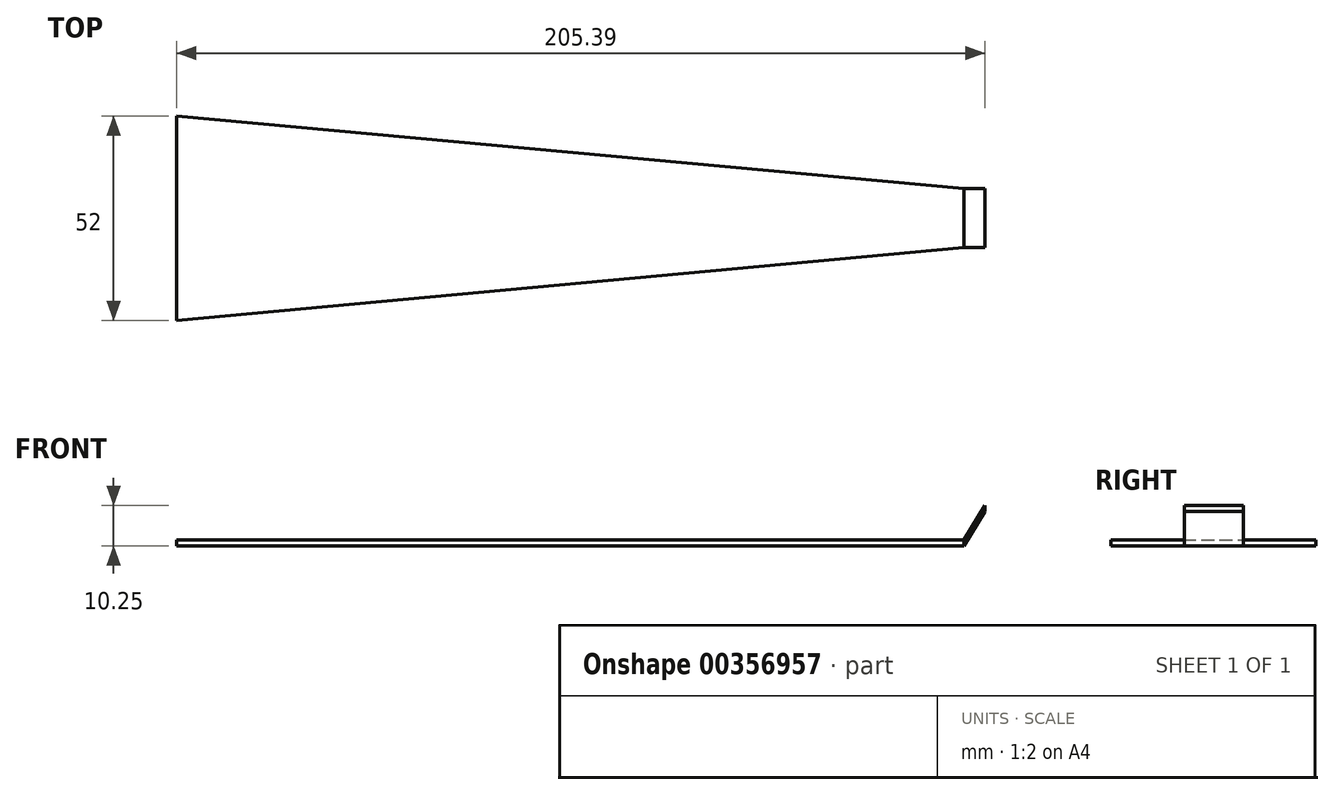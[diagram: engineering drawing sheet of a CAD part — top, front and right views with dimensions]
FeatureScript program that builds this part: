
annotation { "Feature Type Name" : "Feature", "Feature Type Description" : "" }
export const myFeature = defineFeature(function(context is Context, id is Id, definition is map)
    precondition{}
    {
        {
            var Q0;
            Q0=qCreatedBy(makeId("Top.planeOp"),FACE);
            var sketch = newSketch(context, id + "F0", { "sketchPlane" : qUnion([Q0])});
            skLineSegment(sketch, "E0", {"start": v(-40.9, 0) * mm, "end": v(-40.9, 26) * mm, "construction": true});
            skLineSegment(sketch, "E1", {"start": v(-40.9, 26) * mm, "end": v(-40.9, -26) * mm, "construction": true});
            skLineSegment(sketch, "E2", {"start": v(-40.9, -26) * mm, "end": v(159.1, -7.38) * mm, "construction": true});
            skLineSegment(sketch, "E3.MirrorCS", {"start": v(-40.9, 26) * mm, "end": v(159.1, 7.62) * mm, "construction": true});
            skLineSegment(sketch, "E4", {"start": v(-40.9, -26) * mm, "end": v(-40.9, 26) * mm});
            skPoint(sketch, "E5.endSnap0", {"position": v(104.09, 7.3) * mm});
            skLineSegment(sketch, "E6", {"start": v(159.1, -7.38) * mm, "end": v(159.1, 7.62) * mm, "construction": true});
            skLineSegment(sketch, "E7", {"start": v(159.1, -7.38) * mm, "end": v(159.1, 7.62) * mm});
            skPoint(sketch, "E8.orphan", {"position": v(104.09, -24.38) * mm});
            skPoint(sketch, "E9.start.orphan", {"position": v(104.09, 12.68) * mm});
            skPoint(sketch, "E10.trimOffspring.end.orphan", {"position": v(104.09, 38.97) * mm});
            skPoint(sketch, "E11.end.orphan", {"position": v(104.09, -12.32) * mm});
            skPoint(sketch, "E12.end.orphan", {"position": v(104.1, 0) * mm});
            skLineSegment(sketch, "E13", {"start": v(-40.9, -26) * mm, "end": v(159.1, -7.38) * mm});
            skLineSegment(sketch, "E14", {"start": v(-40.9, 26) * mm, "end": v(159.1, 7.62) * mm});
            skPoint(sketch, "E15.orphan", {"position": v(159.1, -36.66) * mm});
            skPoint(sketch, "E16.orphan", {"position": v(-40.9, 40.11) * mm});
            skPoint(sketch, "E17.orphan", {"position": v(-40.9, -31.55) * mm});
            skSolve(sketch);
        }
        {
            var Q0;
            Q0 = qSketchRegion(id + "F0", true);
            extrude(context, id + "F1", {"entities" : qUnion([Q0]), "depth" : 1.5 * mm});
        }
        {
            var Q0;
            Q0=qCreatedBy(makeId("Front.planeOp"),FACE);
            var sketch = newSketch(context, id + "F2", { "sketchPlane" : qUnion([Q0])});
            skPoint(sketch, "E18", {"position": v(159.1, 0) * mm});
            skLineSegment(sketch, "E19", {"start": v(159.1, 0) * mm, "end": v(164.49, 8.75) * mm});
            skSolve(sketch);
        }
        {
            var Q0;
            Q0=makeQuery(id+"F1.opExtrude","SWEPT_FACE",FACE,{"disambiguationData":[OSD([sQuery(id+"F0.wireOp",EDGE,"E7")])]});
            var Q1;
            Q1=sQuery(id+"F2.wireOp",EDGE,"E19");
            sweep(context, id + "F3", {"operationType" : NewBodyOperationType.ADD, "profiles" : qUnion([Q0]), "path" : qUnion([Q1])});
        }
    });
